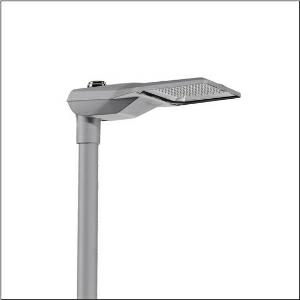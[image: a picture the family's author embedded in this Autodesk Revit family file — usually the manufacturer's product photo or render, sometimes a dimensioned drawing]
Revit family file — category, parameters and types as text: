
# Revit family: streetlight_sl_21_midi___stw1_0a_5xe7e47n08lb_5353
name_source: partatom
category: Lighting Fixtures
units: mm (PartAtom-declared; Revit-internal decimal feet)

## family parameters
Cut with Voids When Loaded = No
Host = Face
Light Source = No
Part Type = Normal
Room Calculation Point = No
Round Connector Dimension = Use Diameter
Shared = No

## types (1)
- --- (1 x LED, 14950 lm, 98.3 W, 4000K)
    Apparent Load = 98 VA
    CIE Flux Codes = 38 75 98 100 100
    Color Rendering = 70
    Color Temperature = 4000K
    Default Elevation = 1800 mm
    Description = Streetlight SL 21 midi, mast luminaire, primary light control with lens, of PMMA, primary optical cover: cover, of toughened safety glass, transparent, light distribution: STW1.0a, light emission: direct distribution, primary light characteristic: asymmetric, installation type: side-entry, LED, 3G 2.5mm², High Power LED, rated luminous flux: 14.950lm, luminous efficacy: 152lm/W, light colour: 740, colour temperature: 4000K, control gear: NEMA (7pin), control: overheat protection, pre-setting: linear dimming characteristic, constant luminous flux control, time-dependent luminous flux control, flexible luminous flux parameterisation, mains connection: 220..240V, AC, 50/60Hz, connection cable pre-assembled, cable length: 10,5m, wiring characteristics: H05VV-F, start of lifetime: 98W, end of service life: 101W, reduction: 45W, luminaire housing, of diecast aluminium (EN AC-44300), powder-coated, SITECO metallic grey (DB 702S), corrosivity category C5 high according to DIN EN ISO 12944, multi-level sealing system, sealing non-destructively replaceable, inclination adjustable: 0°, 5°, 10°, 15°, length: 644mm, width: 335mm, height: 110mm, spigot size: 42mm (side-entry), mounting height: 4..8m, protection rating (complete): IP66, insulation class (complete): insulation class I (protective earthing), certification: CE, ENEC, ENEC+, VDE, impact resistance: IK10, permissible operating ambient temperature for outdoor applications: -40..+50°C, standard-compliant lighting for roads and squares, packaging unit: 1 piece

Light Distribution: STW1.0a
    Height = 111 mm
    Lamp = 1 x LED
    Lamp Light Flux = 14950 lm
    Lamp Power = 98.3 W
    Lamp count = 1
    Length = 644 mm
    Luminous efficacy = 152 lm/W
    Manufacturer = Siteco
    ModVariant = No
    Model = 5XE7E47N08LB
    Number of Poles = 1
    OnlyDefault = Yes
    Power Factor = 1
    Product Name = Streetlight SL 21 midi | STW1.0a
    Product group = mast luminaire | pylon top
    ProductGroupID = 6100
    Protection Class = Protection class I
    Protection Degree = IP 66
    RLX_Detail_Level = 1
    RLX_Emergency_Light_Flux = 0 lm
    RLX_Emergency_Type = 0
    RLX_Emergency_Type_DB = No
    RlxData = <blob elided: 26745 chars, md5=5d538c64>
    Socket = socket
    Standby Power = 0 W
    System Light Flux = 14950 lm
    System Power = 98 W
    Type Comments = factory setting: luminous flux: 100 % | dim-lin: 254 | 1020 mA
    Type Image = l_1294377.jpg
    URL = http://relux.com
    VarID = @adj_134975
    Voltage = 0 V
    Weight = 0.00 kg
    Width = 336 mm

## geometry (parser evidence)
native form markers: Blend x4, Sweep x11
no freeform markers — native parametric forms only
